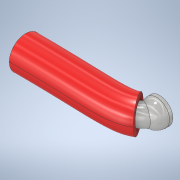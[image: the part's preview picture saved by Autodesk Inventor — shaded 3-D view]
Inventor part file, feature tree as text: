
AUTODESK INVENTOR PART (.ipt)
format: ipt  version: 2020.1 (Build 241239000, 239)  size: 276,992 bytes
history: native  units: mm
features: sketch x6, sweep x2, extrude x1, fillet x1, plane x1
ambient origin geometry x8: Origin, YZ Plane, XZ Plane, XY Plane, X Axis, Y Axis, Z Axis, Center Point
bodies: Solid1 (feature_tree)
feature tree (11):
  extrude  "Extrusion1"  Depth=2.5mm TaperAngle=0.0deg
  fillet  "Fillet1"  Radius=2.0mm
  sweep  "Sweep1"
  plane  "Work Plane1"
  sweep  "Sweep4"
  sketch  "Sketch6"  dims[d19=-2.0mm d20=0.0mm d21=0.0mm]
  sketch  "Sketch1"  dims[d0=4.0mm d1=2.5mm d2=0.0mm d3=2.0mm]
  sketch  "Sketch2"  dims[d4=2.6mm d5=3.06mm]
  sketch  "Sketch3"  dims[d6=0.0mm d7=0.0mm d9=5.0mm]
  sketch  "Sketch4"  dims[d18=4.0mm]
  sketch  "3D Sketch1"
